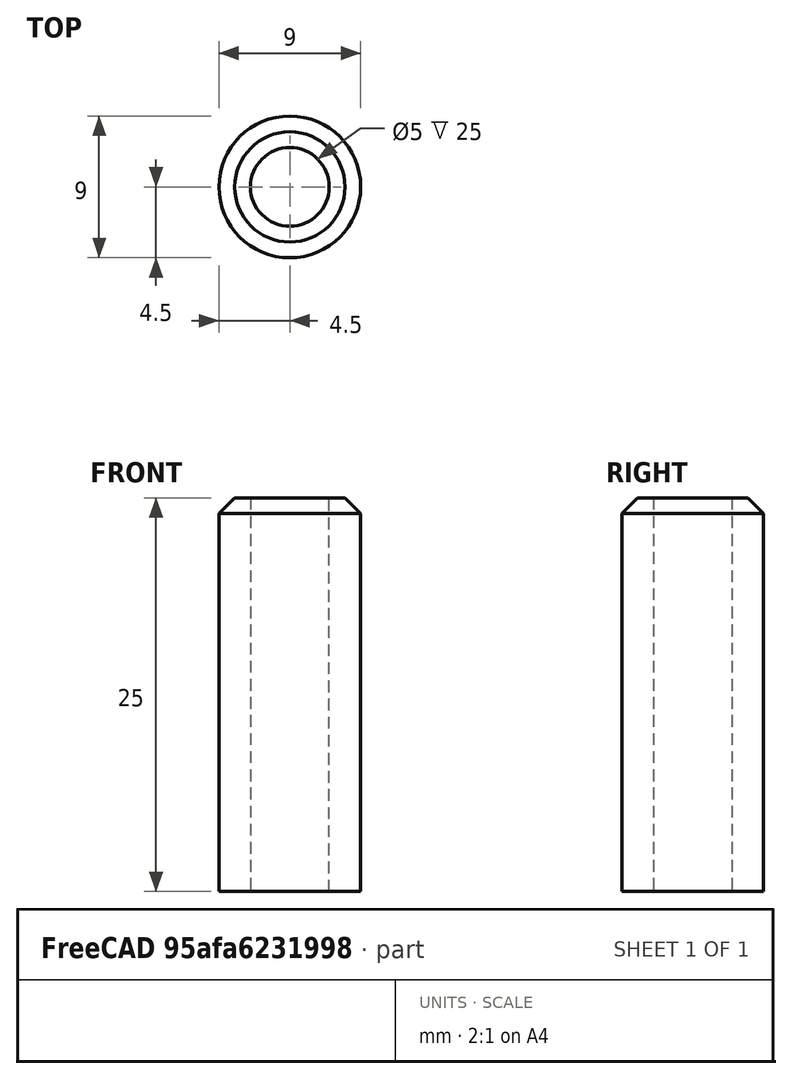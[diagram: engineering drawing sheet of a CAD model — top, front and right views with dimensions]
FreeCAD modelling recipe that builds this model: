
FCSTD DOCUMENT  (FreeCAD 0.19R24276 (Git))
Label: part_of_val_M9x25
License: All rights reserved
LicenseURL: http://en.wikipedia.org/wiki/All_rights_reserved
objects: Sketcher::SketchObject×1, PartDesign::Pad×1, PartDesign::Chamfer×1, PartDesign::Body×1
note: 6 computed .brp shape members not serialized (recipe doc carries the construction recipe); baked Part::Feature solids carry a one-line shape summary decoded from their .brp

FEATURE [Sketcher::SketchObject] Sketch
  FullyConstrained = true
  MapMode = 5
  Support = -> [XY_Plane]
  sketch-geometry (2):
    g0: Circle CenterX=0 CenterY=0 CenterZ=0 NormalX=0 NormalY=0 NormalZ=1 AngleXU=0 Radius=4.5
    g1: Circle CenterX=0 CenterY=0 CenterZ=0 NormalX=0 NormalY=0 NormalZ=1 AngleXU=0 Radius=2.5
  constraints (4):
    c: Diameter(g0) = 9
    c: Coincident(g0,g-1)
    c: Coincident(g1,g0)
    c: Diameter(g1) = 5
FEATURE [PartDesign::Pad] Pad
  Direction = (1,1,1)
  Length = 25
  Length2 = 100
  Profile = -> Sketch
  Type = 0
FEATURE [PartDesign::Chamfer] Chamfer
  Angle = 45
  Base = -> Pad [Edge3]
  BaseFeature = -> Pad
  ChamferType = 0
  FlipDirection = false
  Size = 1
  Size2 = 1
  SupportTransform = false
FEATURE [PartDesign::Body] Body
  Group = -> [Sketch,Pad,Chamfer]
  Origin = -> Origin
  Tip = -> Chamfer
